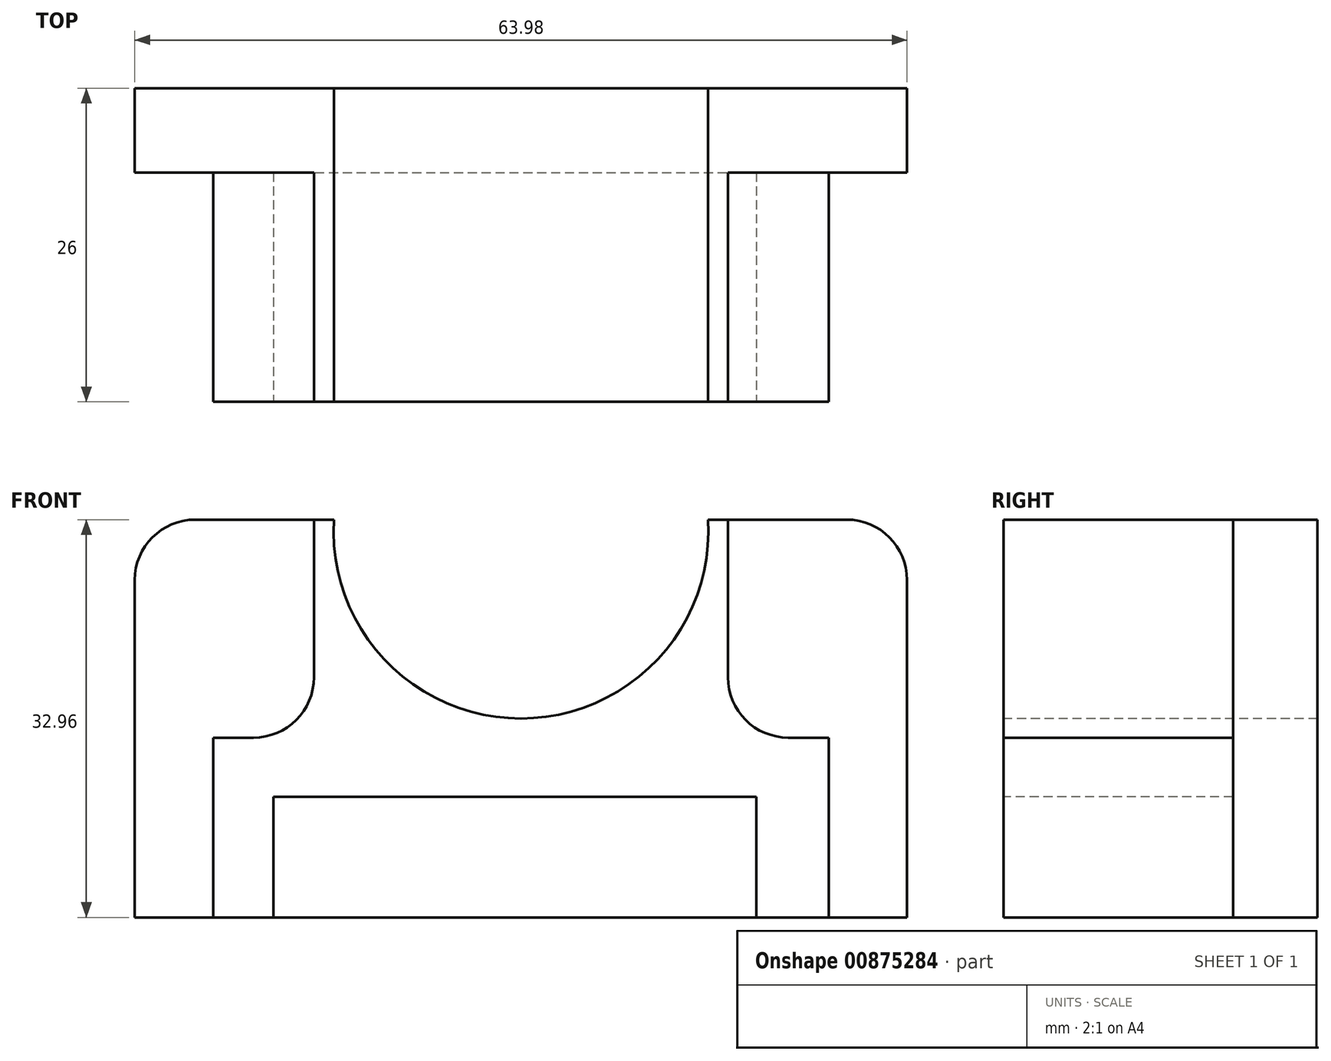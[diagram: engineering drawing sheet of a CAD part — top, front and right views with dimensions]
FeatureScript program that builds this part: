
annotation { "Feature Type Name" : "Feature", "Feature Type Description" : "" }
export const myFeature = defineFeature(function(context is Context, id is Id, definition is map)
    precondition{}
    {
        {
            var Q0;
            Q0=qCreatedBy(makeId("Front.planeOp"),FACE);
            var sketch = newSketch(context, id + "F0", { "sketchPlane" : qUnion([Q0])});
            skLineSegment(sketch, "E0.bottom", {"start": v(-31.99, 16.48) * mm, "end": v(31.99, 16.48) * mm});
            skLineSegment(sketch, "E0.top", {"start": v(-31.99, -16.48) * mm, "end": v(31.99, -16.48) * mm});
            skLineSegment(sketch, "E0.left", {"start": v(-31.99, 16.48) * mm, "end": v(-31.99, -16.48) * mm});
            skLineSegment(sketch, "E0.right", {"start": v(31.99, 16.48) * mm, "end": v(31.99, -16.48) * mm});
            skPoint(sketch, "E0.middle", {"position": v(0, 0) * mm});
            skSolve(sketch);
        }
        {
            var Q0;
            Q0 = qSketchRegion(id + "F0", true);
            extrude(context, id + "F1", {"entities" : qUnion([Q0]), "depth" : 7 * mm, "offsetDistance" : 25 * mm});
        }
        {
            var Q0;
            Q0=makeQuery(id+"F1.opExtrude","CAP_FACE",FACE,{"disambiguationData":[OSD([sQuery(id+"F0.wireOp",EDGE,"E0.bottom"),sQuery(id+"F0.wireOp",EDGE,"E0.top"),sQuery(id+"F0.wireOp",EDGE,"E0.left"),sQuery(id+"F0.wireOp",EDGE,"E0.right")])],"isStart":false});
            var sketch = newSketch(context, id + "F2", { "sketchPlane" : qUnion([Q0])});
            skLineSegment(sketch, "E1.bottom", {"start": v(-25.5, -16.48) * mm, "end": v(25.5, -16.48) * mm});
            skLineSegment(sketch, "E1.top", {"start": v(-25.5, 16.48) * mm, "end": v(25.5, 16.48) * mm});
            skLineSegment(sketch, "E1.left", {"start": v(-25.5, -16.48) * mm, "end": v(-25.5, 16.48) * mm});
            skLineSegment(sketch, "E1.right", {"start": v(25.5, -16.48) * mm, "end": v(25.5, 16.48) * mm});
            skPoint(sketch, "E1.middle", {"position": v(0, 0) * mm});
            skSolve(sketch);
        }
        {
            var Q0;
            Q0 = qSketchRegion(id + "F2", true);
            extrude(context, id + "F3", {"entities" : qUnion([Q0]), "operationType" : NewBodyOperationType.ADD, "depth" : 19 * mm, "offsetDistance" : 25 * mm});
        }
        {
            var Q0;
            Q0=makeQuery(id+"F3.opExtrude","CAP_FACE",FACE,{"disambiguationData":[OSD([sQuery(id+"F2.wireOp",EDGE,"E1.bottom"),sQuery(id+"F2.wireOp",EDGE,"E1.top"),sQuery(id+"F2.wireOp",EDGE,"E1.left"),sQuery(id+"F2.wireOp",EDGE,"E1.right")])],"isStart":false});
            var sketch = newSketch(context, id + "F4", { "sketchPlane" : qUnion([Q0])});
            skLineSegment(sketch, "E2.bottom", {"start": v(-20.5, -6.48) * mm, "end": v(19.5, -6.48) * mm});
            skLineSegment(sketch, "E2.top", {"start": v(-20.5, -16.48) * mm, "end": v(19.5, -16.48) * mm});
            skLineSegment(sketch, "E2.left", {"start": v(-20.5, -6.48) * mm, "end": v(-20.5, -16.48) * mm});
            skLineSegment(sketch, "E2.right", {"start": v(19.5, -6.48) * mm, "end": v(19.5, -16.48) * mm});
            skSolve(sketch);
        }
        {
            var Q0;
            Q0 = qSketchRegion(id + "F4", true);
            extrude(context, id + "F5", {"entities" : qUnion([Q0]), "operationType" : NewBodyOperationType.REMOVE, "oppositeDirection" : true, "depth" : 19 * mm, "offsetDistance" : 25 * mm});
        }
        {
            var Q0;
            Q0=makeQuery(id+"F3.opExtrude","CAP_FACE",FACE,{"disambiguationData":[OSD([sQuery(id+"F2.wireOp",EDGE,"E1.bottom"),sQuery(id+"F2.wireOp",EDGE,"E1.top"),sQuery(id+"F2.wireOp",EDGE,"E1.left"),sQuery(id+"F2.wireOp",EDGE,"E1.right")])],"isStart":false});
            var sketch = newSketch(context, id + "F6", { "sketchPlane" : qUnion([Q0])});
            skArc(sketch, "E3", {"start": v(-15.5, 16.48) * mm, "mid": v(0, 0) * mm, "end": v(15.5, 16.48) * mm});
            skSolve(sketch);
        }
        {
            var Q0;
            {var subQ0=sQuery(id+"F6.wireOp",EDGE,"E3");Q0=makeQuery(id+"F6.imprint","IMPRINT",FACE,{"disambiguationData":[TD([[makeQuery(id+"F6.imprint","IMPRINT",EDGE,{"derivedFrom":subQ0}),1.0]])]});}
            extrude(context, id + "F7", {"entities" : qUnion([Q0]), "operationType" : NewBodyOperationType.REMOVE, "oppositeDirection" : true, "depth" : 47.2 * mm, "offsetDistance" : 25 * mm});
        }
        {
            var Q0;
            Q0=makeQuery(id+"F1.opExtrude","SWEPT_EDGE",EDGE,{"disambiguationData":[OSD([sQuery(id+"F0.wireOp",EDGE,"E0.bottom"),sQuery(id+"F0.wireOp",EDGE,"E0.right")])]});
            var Q1;
            Q1=makeQuery(id+"F1.opExtrude","SWEPT_EDGE",EDGE,{"disambiguationData":[OSD([sQuery(id+"F0.wireOp",EDGE,"E0.bottom"),sQuery(id+"F0.wireOp",EDGE,"E0.left")])]});
            fillet(context, id + "F8", {"entities" : qUnion([Q0, Q1]), "radius" : 5 * mm, "tangentPropagation" : true, "allowEdgeOverflow" : false});
        }
        {
            var Q0;
            Q0=makeQuery(id+"F3.opExtrude","CAP_FACE",FACE,{"disambiguationData":[OSD([sQuery(id+"F2.wireOp",EDGE,"E1.bottom"),sQuery(id+"F2.wireOp",EDGE,"E1.top"),sQuery(id+"F2.wireOp",EDGE,"E1.left"),sQuery(id+"F2.wireOp",EDGE,"E1.right")])],"isStart":false});
            var sketch = newSketch(context, id + "F9", { "sketchPlane" : qUnion([Q0])});
            skLineSegment(sketch, "E4.bottom", {"start": v(-25.5, 16.48) * mm, "end": v(-17.15, 16.48) * mm});
            skLineSegment(sketch, "E4.top", {"start": v(-25.5, -1.59) * mm, "end": v(-17.15, -1.59) * mm});
            skLineSegment(sketch, "E4.left", {"start": v(-25.5, 16.48) * mm, "end": v(-25.5, -1.59) * mm});
            skLineSegment(sketch, "E4.right", {"start": v(-17.15, 16.48) * mm, "end": v(-17.15, -1.59) * mm});
            skLineSegment(sketch, "E5.MirrorCS", {"start": v(17.15, 16.48) * mm, "end": v(17.15, -1.59) * mm});
            skLineSegment(sketch, "E6.MirrorCS", {"start": v(25.5, -1.59) * mm, "end": v(17.15, -1.59) * mm});
            skLineSegment(sketch, "E7.MirrorCS", {"start": v(25.5, 16.48) * mm, "end": v(25.5, -1.59) * mm});
            skLineSegment(sketch, "E8.MirrorCS", {"start": v(25.5, 16.48) * mm, "end": v(17.15, 16.48) * mm});
            skSolve(sketch);
        }
        {
            var Q0;
            Q0 = qSketchRegion(id + "F9", true);
            extrude(context, id + "F10", {"entities" : qUnion([Q0]), "operationType" : NewBodyOperationType.REMOVE, "oppositeDirection" : true, "depth" : 19 * mm, "offsetDistance" : 25 * mm});
        }
        {
            var Q0;
            Q0=makeQuery(id+"F10.boolean.opBoolean","COPY",EDGE,{"derivedFrom":makeQuery(id+"F10.opExtrude","SWEPT_EDGE",EDGE,{"disambiguationData":[OSD([sQuery(id+"F9.wireOp",EDGE,"E4.top"),sQuery(id+"F9.wireOp",EDGE,"E4.right")])]})});
            var Q1;
            Q1=makeQuery(id+"F10.boolean.opBoolean","COPY",EDGE,{"derivedFrom":makeQuery(id+"F10.opExtrude","SWEPT_EDGE",EDGE,{"disambiguationData":[OSD([sQuery(id+"F9.wireOp",EDGE,"E5.MirrorCS"),sQuery(id+"F9.wireOp",EDGE,"E6.MirrorCS")])]})});
            fillet(context, id + "F11", {"entities" : qUnion([Q0, Q1]), "radius" : 5 * mm, "tangentPropagation" : true, "allowEdgeOverflow" : false});
        }
    });
